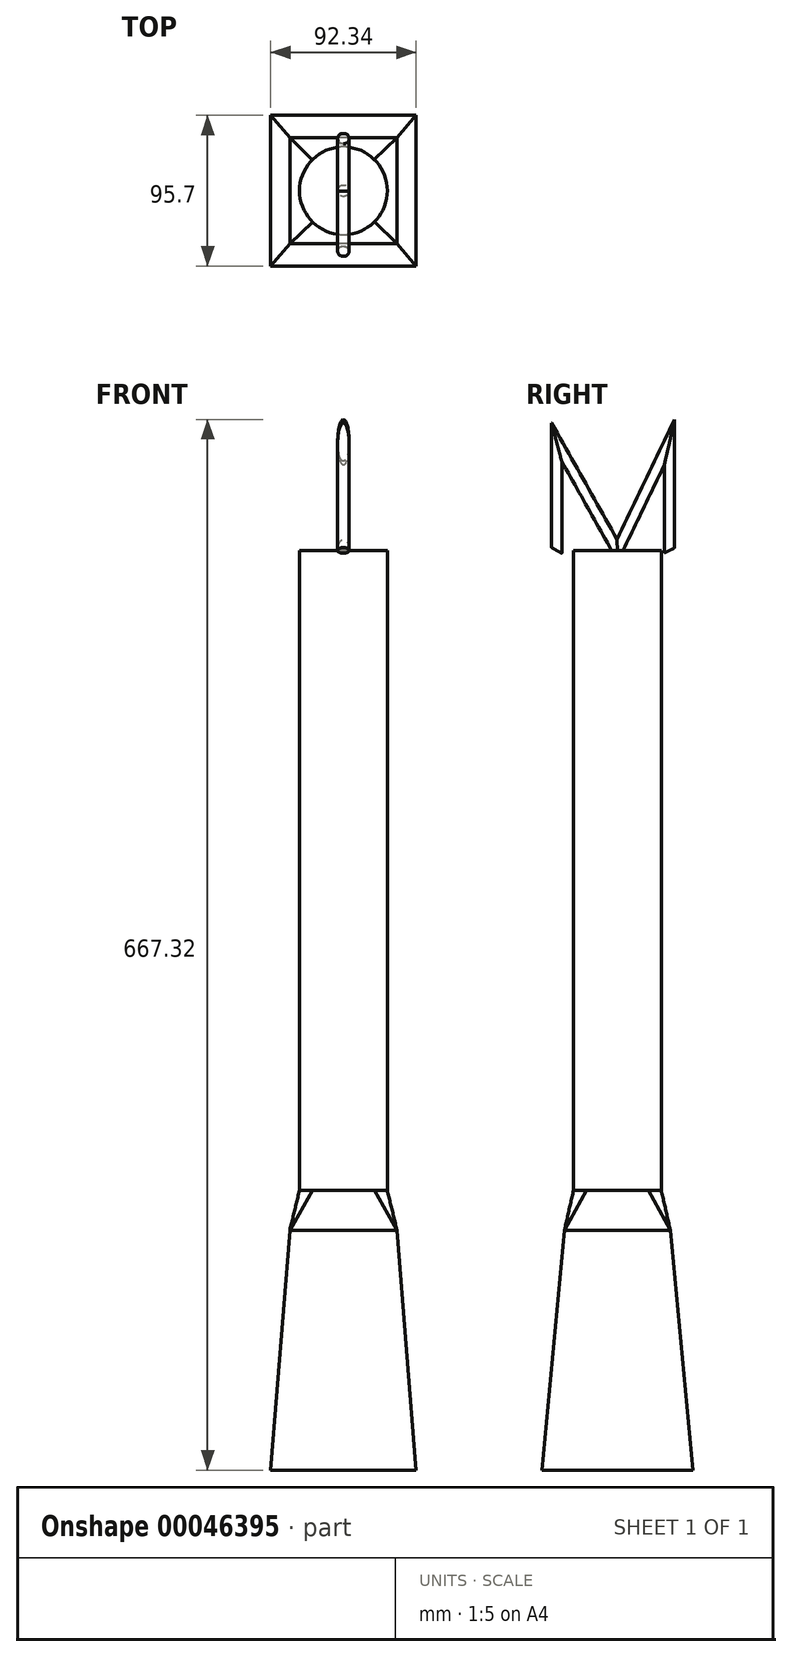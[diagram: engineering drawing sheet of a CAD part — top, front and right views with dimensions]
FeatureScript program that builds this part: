
annotation { "Feature Type Name" : "Feature", "Feature Type Description" : "" }
export const myFeature = defineFeature(function(context is Context, id is Id, definition is map)
    precondition{}
    {
        {
            var Q0;
            Q0=qCreatedBy(makeId("Top.planeOp"),FACE);
            var sketch = newSketch(context, id + "F0", { "sketchPlane" : qUnion([Q0])});
            skCircle(sketch, "E0", {"center": v(0, 0) * mm, "radius": 27.87 * mm});
            skSolve(sketch);
        }
        {
            var Q0;
            Q0 = qSketchRegion(id + "F0", true);
            extrude(context, id + "F1", {"entities" : qUnion([Q0]), "endBound" : BoundingType.SYMMETRIC, "oppositeDirection" : true, "depth" : 254 * mm});
        }
        {
            var Q0;
            Q0=makeQuery(id+"F1.opExtrude","CAP_FACE",FACE,{"disambiguationData":[OSD([sQuery(id+"F0.wireOp",EDGE,"E0")])],"isStart":false});
            cPlane(context, id + "F2", {"entities" : qUnion([Q0]), "cplaneType" : CPlaneType.OFFSET, "offset" : 25.4 * mm, "width" : 152.4 * mm, "height" : 152.4 * mm});
        }
        {
            var Q0;
            Q0=qCreatedBy(id+"F2.planeOp",FACE);
            var sketch = newSketch(context, id + "F3", { "sketchPlane" : qUnion([Q0])});
            skLineSegment(sketch, "E1.rect.bottom", {"start": v(34.02, 33.61) * mm, "end": v(-34.02, 33.61) * mm});
            skLineSegment(sketch, "E1.rect.top", {"start": v(34.02, -33.61) * mm, "end": v(-34.02, -33.61) * mm});
            skLineSegment(sketch, "E1.rect.left", {"start": v(34.02, 33.61) * mm, "end": v(34.02, -33.61) * mm});
            skLineSegment(sketch, "E1.rect.right", {"start": v(-34.02, 33.61) * mm, "end": v(-34.02, -33.61) * mm});
            skPoint(sketch, "E1.rect.middle", {"position": v(0, 0) * mm});
            skSolve(sketch);
        }
        {
            var Q0;
            Q0=makeQuery(id+"F1.opExtrude","CAP_FACE",FACE,{"disambiguationData":[OSD([sQuery(id+"F0.wireOp",EDGE,"E0")])],"isStart":false});
            var Q1;
            Q1 = qSketchRegion(id + "F3", true);
            loft(context, id + "F4", {"sheetProfilesArray" : [{ "sheetProfileEntities" : qUnion([Q0]) }, { "sheetProfileEntities" : qUnion([Q1]) }]});
        }
        {
            var Q0;
            Q0=qCreatedBy(id+"F2.planeOp",FACE);
            cPlane(context, id + "F5", {"entities" : qUnion([Q0]), "cplaneType" : CPlaneType.OFFSET, "offset" : 152.4 * mm, "width" : 152.4 * mm, "height" : 152.4 * mm});
        }
        {
            var Q0;
            Q0=qCreatedBy(id+"F5.planeOp",FACE);
            var sketch = newSketch(context, id + "F6", { "sketchPlane" : qUnion([Q0])});
            skLineSegment(sketch, "E2.rect.bottom", {"start": v(46.17, -47.85) * mm, "end": v(-46.17, -47.85) * mm});
            skLineSegment(sketch, "E2.rect.top", {"start": v(46.17, 47.85) * mm, "end": v(-46.17, 47.85) * mm});
            skLineSegment(sketch, "E2.rect.left", {"start": v(46.17, -47.85) * mm, "end": v(46.17, 47.85) * mm});
            skLineSegment(sketch, "E2.rect.right", {"start": v(-46.17, -47.85) * mm, "end": v(-46.17, 47.85) * mm});
            skPoint(sketch, "E2.rect.middle", {"position": v(0, 0) * mm});
            skSolve(sketch);
        }
        {
            var Q1;
            Q1=makeQuery(id+"F6.imprint","IMPRINT",FACE,{"disambiguationData":[TD([[makeQuery(id+"F6.imprint","IMPRINT",EDGE,{"derivedFrom":sQuery(id+"F6.wireOp",EDGE,"E2.rect.bottom")}),-1.0]])]});
            var Q2;
            Q2=makeQuery(id+"F4.opLoft","CAP_FACE",FACE,{"disambiguationData":[OSD([makeQuery(id+"F3.imprint","IMPRINT",FACE,{"disambiguationData":[TD([[makeQuery(id+"F3.imprint","IMPRINT",EDGE,{"derivedFrom":sQuery(id+"F3.wireOp",EDGE,"E1.rect.bottom")}),1.0]])]})])],"isStart":true});
            loft(context, id + "F7", {"operationType" : NewBodyOperationType.ADD, "sheetProfilesArray" : [{ "sheetProfileEntities" : qUnion([Q1]) }, { "sheetProfileEntities" : qUnion([Q2]) }]});
        }
        {
            var Q0;
            Q0=makeQuery(id+"F1.opExtrude","CAP_FACE",FACE,{"disambiguationData":[OSD([sQuery(id+"F0.wireOp",EDGE,"E0")])],"isStart":true});
            extrude(context, id + "F8", {"entities" : qUnion([Q0]), "operationType" : NewBodyOperationType.ADD, "depth" : 152.4 * mm});
        }
        {
            var Q0;
            Q0=makeQuery(id+"F8.opExtrude","CAP_EDGE",EDGE,{"disambiguationData":[OSD([sQuery(id+"F0.wireOp",EDGE,"E0")])],"isStart":false});
            cPlane(context, id + "F9", {"entities" : qUnion([Q0]), "cplaneType" : CPlaneType.LINE_ANGLE, "offset" : 152.4 * mm, "angle" : 0 * degree, "width" : 152.4 * mm, "height" : 152.4 * mm});
        }
        {
            var Q0;
            Q0=qCreatedBy(id+"F9.planeOp",FACE);
            var sketch = newSketch(context, id + "F10", { "sketchPlane" : qUnion([Q0])});
            skLineSegment(sketch, "E3", {"start": v(0, 279.38) * mm, "end": v(-38.53, 348.04) * mm});
            skLineSegment(sketch, "E4", {"start": v(-38.53, 348.04) * mm, "end": v(-38.53, 279.38) * mm});
            skLineSegment(sketch, "E5", {"start": v(0, 279.38) * mm, "end": v(33.06, 348.04) * mm});
            skLineSegment(sketch, "E6", {"start": v(33.06, 348.04) * mm, "end": v(33.06, 279.38) * mm});
            skSolve(sketch);
        }
        {
            var Q0;
            Q0=makeQuery(id+"F8.opExtrude","CAP_FACE",FACE,{"disambiguationData":[OSD([sQuery(id+"F0.wireOp",EDGE,"E0")])],"isStart":false});
            var sketch = newSketch(context, id + "F11", { "sketchPlane" : qUnion([Q0])});
            skCircle(sketch, "E7", {"center": v(0, 0) * mm, "radius": 3.66 * mm});
            skSolve(sketch);
        }
        {
            var Q0;
            Q0=makeQuery(id+"F11.imprint","IMPRINT",FACE,{"disambiguationData":[TD([[makeQuery(id+"F11.imprint","IMPRINT",EDGE,{"derivedFrom":sQuery(id+"F11.wireOp",EDGE,"E7")}),1.0]])]});
            var Q1;
            Q1=sQuery(id+"F10.wireOp",EDGE,"E5");
            var Q2;
            Q2=sQuery(id+"F10.wireOp",EDGE,"E6");
            sweep(context, id + "F12", {"operationType" : NewBodyOperationType.ADD, "profiles" : qUnion([Q0]), "path" : qUnion([Q1, Q2])});
        }
        {
            var Q0;
            Q0 = qSketchRegion(id + "F11", true);
            var Q1;
            Q1=sQuery(id+"F10.wireOp",EDGE,"E3");
            var Q2;
            Q2=sQuery(id+"F10.wireOp",EDGE,"E4");
            sweep(context, id + "F13", {"operationType" : NewBodyOperationType.ADD, "profiles" : qUnion([Q0]), "path" : qUnion([Q1, Q2])});
        }
    });
